# Revit family: Drain_Trench_11.25_Inch_Wide-Zurn-Z668-Heavy-Duty
name_source: partatom
category: Plumbing Fixtures
units: mm (PartAtom-declared; Revit-internal decimal feet)

## family parameters
Always vertical = Yes
Cut with Voids When Loaded = No
Maintain Annotation Orientation = No
OmniClass Number = 23.70.50.21.24.14
OmniClass Title = Deck Waste Water Drains
Part Type = Normal
Room Calculation Point = No
Round Connector Dimension = Use Radius
Shared = No
Work Plane-Based = No

## types (7) — shared parameters
Approx. Weight (Lbs) = 115 "
Assembly Code = D2030300
CW Connection = No
Default Elevation = 2 "
Description = 11-1/4 x 19-1/4 [286 X 489] HEAVY-DUTY DRAIN
Grate Material = Iron - Zurn - Cast - Painted - Blue
Grate Open Area (Sq. In.) = 60 SF
HW Connection = No
Main Material = Iron - Zurn - Cast - Painted - Blue
Manufacturer = Zurn Water, LLC
Manufacurer Brand = Zurn
Model = Z668
Modified Date = 12/08/25
Product Documentation Link = https://files.zurn.com
Product Page URL = https://www.zurn.com
Product data url = https://www.bimobject.com
URL = www.zurn.com
Vent Connection = No
WFU = 1
Waste Connection = Yes
zero-valued in all types: CWFU, HWFU

## per-type parameters (varying)
| type | A_ Pipe Size (Inner Diameter) | A_ Pipe Size (Nominal Diameter) | A_ Pipe Size (Nominal Radius) | A_ Pipe Size (Outer Diameter) | Body Height 'E' | Type Comments |
| Z668-4IC | 4.026 " | 4 " | 2 " | 4.5 " | 10.25 " | Z668 4 Inch Inside Caulk Outlet |
| Z668-6IC | 6.065 " | 6 " | 3 " | 6.625 " | 10.25 " | Z668 6 Inch Inside Caulk Outlet |
| Z668-4IP | 4.026 " | 4 " | 2 " | 4.5 " | 8.625 " | Z668 4 Inch Threaded Outlet |
| Z668-6IP | 6.065 " | 6 " | 3 " | 6.625 " | 8.625 " | Z668 6 Inch Threaded Outlet |
| Z668-4NH | 4.026 " | 4 " | 2 " | 4.5 " | 11.125 " | Z668 4 Inch No-Hub Outlet |
| Z668-6NH | 6.065 " | 6 " | 3 " | 6.625 " | 11.125 " | Z668 6 Inch No-Hub Outlet |
| Z668-4NL | 4.026 " | 4 " | 2 " | 4.5 " | 9.5 " | Z668 4 Inch Neo-Loc Outlet |

## geometry (parser evidence)
native form markers: Blend x20, Sweep x9
no freeform markers — native parametric forms only
